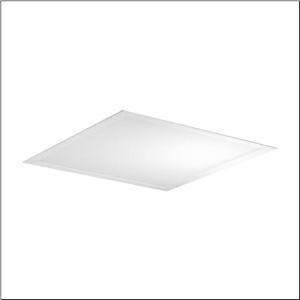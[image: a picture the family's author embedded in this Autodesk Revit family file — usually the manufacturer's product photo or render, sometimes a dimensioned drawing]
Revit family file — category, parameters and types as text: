
# Revit family: apollon_r__21_square_51mq11w72313_e9b2
name_source: partatom
category: Lighting Fixtures
units: mm (PartAtom-declared; Revit-internal decimal feet)

## family parameters
Cut with Voids When Loaded = No
Host = Face
Light Source = No
Part Type = Normal
Room Calculation Point = No
Round Connector Dimension = Use Diameter
Shared = No

## types (1)
- Apollon® 21 square (1 x LED, 4000 lm, 33 W, 3000K)
    Apparent Load = 33 VA
    CIE Flux Codes = 61 87 97 100 100
    Color Rendering = 80
    Color Temperature = 3000K
    Default Elevation = 1800 mm
    Description = Apollon® 21 square, office luminaire, primary optical cover: micro prismatic cover, of PMMA, CAT 2 (L<= 3000cd/m²), light emission: direct distribution, primary light characteristic: symmetric, installation type: lay-in mounting, LED, rated luminous flux: 4.000lm, luminous efficacy: 121lm/W, light colour: 830, colour temperature: 3000K, control gear: ECG, with terminal, 3-pole, mains connection: 220..240V, AC, 50/60Hz, rated input power: 33W, housing, of aluminium, traffic white (RAL 9016), module: M625, length: 620mm, width: 620mm, height: 40mm, housing upper side, of sheet steel, galvanised, protection rating (complete): IP20, protection rating (lamp compartment, on room side): IP50, insulation class (complete): insulation class II (safety insulation), certification: CE, ENEC, permissible operating ambient temperature: -20..+40°C, packaging unit: 1 piece
    Height = 0 mm  [stored 0 ft]
    Lamp = 1 x LED
    Lamp Light Flux = 4000 lm
    Lamp Power = 33 W
    Lamp count = 1
    Length = 620 mm
    Luminous efficacy = 121 lm/W
    Manufacturer = Siteco
    ModVariant = No
    Model = 51MQ11W72313
    Mounting Place = Ceiling
    Mounting Type = Recessed
    Number of Poles = 1
    OnlyDefault = Yes
    Power Factor = 1
    Product Name = Apollon® 21 square
    Product group = office luminaire | ceiling recessed
    ProductGroupID = 401
    Protection Class = Protection class II
    Protection Degree = IP 20
    RLX_Detail_Level = 1
    RLX_Emergency_Light_Flux = 0 lm
    RLX_Emergency_Type = 0
    RLX_Emergency_Type_DB = No
    RlxData = <blob elided: 14901 chars, md5=4c890aa1>
    Socket = socket
    Standby Power = 0 W
    System Light Flux = 4000 lm
    System Power = 33 W
    Type Comments = Product without accessories
    Type Image = l_1291054.jpg
    URL = http://relux.com
    VarID = ---
    Voltage = 0 V
    Weight = 0.00 kg
    Width = 620 mm

note: [stored X ft] marks values corroborated as IEEE doubles in the binary element streams (Revit-internal decimal feet)

## geometry (parser evidence)
native form markers: Sweep x11
no freeform markers — native parametric forms only
